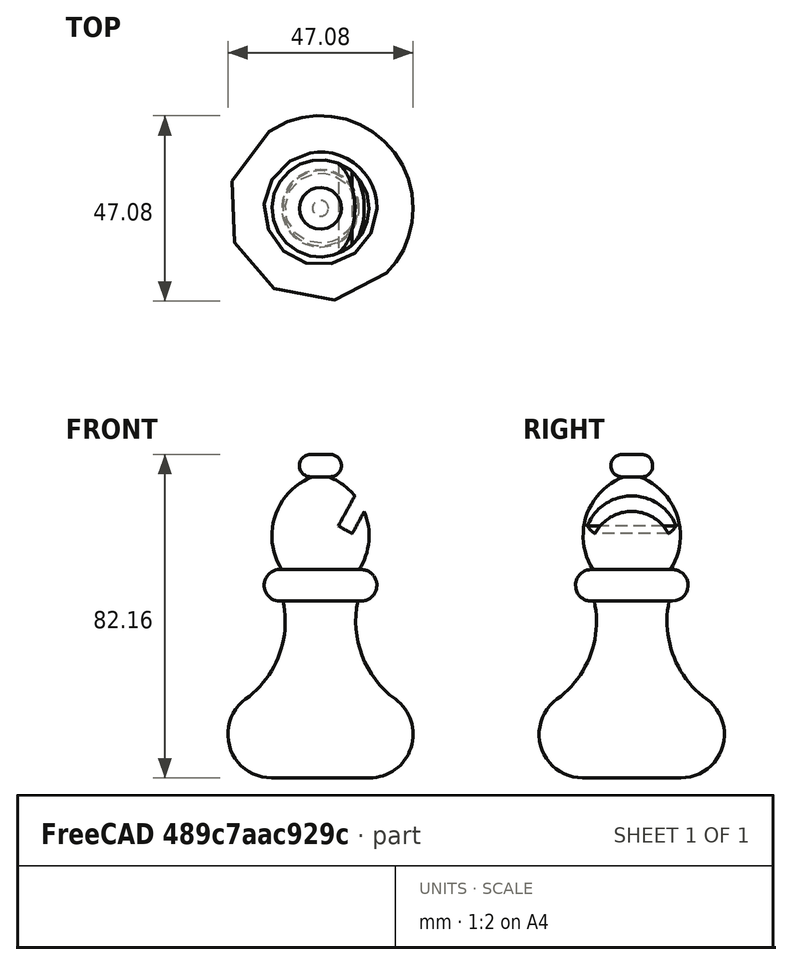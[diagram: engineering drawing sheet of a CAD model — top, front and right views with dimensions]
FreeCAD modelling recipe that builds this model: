
FCSTD DOCUMENT  (FreeCAD 0.16R)
Label: Bishop1
License: All rights reserved
LicenseURL: http://en.wikipedia.org/wiki/All_rights_reserved
objects: Sketcher::SketchObject×2, PartDesign::Revolution×1, PartDesign::Pad×1, Part::Cut×1, Mesh::Feature×1
note: 7 computed .brp shape members not serialized (recipe doc carries the construction recipe); baked Part::Feature solids carry a one-line shape summary decoded from their .brp

FEATURE [Sketcher::SketchObject] Sketch
  Placement = pos=(0,0,0) rot=(-1,0,0;4.71239rad)
  sketch-geometry (9):
    g0: ArcOfCircle CenterX=-3.65574 CenterY=41.525 CenterZ=0 NormalX=0 NormalY=0 NormalZ=1 Radius=16 StartAngle=5.71293 EndAngle=7.49269
    g1: ArcOfCircle CenterX=10.3244 CenterY=28.9203 CenterZ=0 NormalX=0 NormalY=0 NormalZ=1 Radius=4 StartAngle=4.51243 EndAngle=7.98232
    g2: ArcOfCircle CenterX=33.4264 CenterY=19.7584 CenterZ=0 NormalX=0 NormalY=0 NormalZ=1 Radius=24.4646 StartAngle=2.92567 EndAngle=4.08172
    g3: ArcOfCircle CenterX=12.4756 CenterY=-8.93581 CenterZ=0 NormalX=0 NormalY=0 NormalZ=1 Radius=11.0642 StartAngle=4.71239 EndAngle=7.22331
    g4: LineSegment StartX=0 StartY=-20 StartZ=0 EndX=12.4756 EndY=-20 EndZ=0
    g5: ArcOfCircle CenterX=2.5 CenterY=59.3249 CenterZ=0 NormalX=0 NormalY=0 NormalZ=1 Radius=2.8329 StartAngle=4.71239 EndAngle=7.85398
    g6: LineSegment StartX=2 StartY=56.492 StartZ=0 EndX=2.5 EndY=56.492 EndZ=0
    g7: LineSegment StartX=0 StartY=62.1578 StartZ=0 EndX=2.5 EndY=62.1578 EndZ=0
    g8: LineSegment StartX=0 StartY=-20 StartZ=0 EndX=0 EndY=62.1578 EndZ=0
  constraints (26):
    c: Coincident(g2,g1)
    c: Coincident(g2,g3)
    c: Horizontal(g4)
    c: PointOnObject(g4,g-2)
    c: Coincident(g4,g3)
    c: Tangent(g4,g3)
    c: Tangent(g3,g2)
    c: Coincident(g0,g1)
    c: Tangent(g6,g5) = -1.5708
    c: Tangent(g7,g5) = 1.5708
    c: Horizontal(g6)
    c: Coincident(g6,g0)
    c: PointOnObject(g7,g-2)
    c: Vertical(g8)
    c: Coincident(g8,g7)
    c: Coincident(g4,g8)
    c: Horizontal(g7)
    c: Radius(g1) = 4
    c: Radius(g0) = 16
    c: DistanceX(g0) = 2
    c: DistanceX(g2) = 19
    c: PointOnObject(g2,g-1)
    c: DistanceY(g1) = 25
    c: DistanceY(g0) = 32.8874
    c: DistanceX(g5) = 2.5
    c: DistanceY(g4) = -20
FEATURE [PartDesign::Revolution] Revolution
  Angle = 360
  Axis = (0,0,1)
  Base = (0,0,0)
  Placement = pos=(0,0,0) rot=(-1,0,0;4.71239rad)
  ReferenceAxis = -> Sketch [V_Axis]
  Reversed = true
  Sketch = -> Sketch
FEATURE [Sketcher::SketchObject] Sketch001
  Placement = pos=(0,0,0) rot=(-1,0,0;4.71239rad)
  sketch-geometry (4):
    g0: LineSegment StartX=12.4992 StartY=58.5281 StartZ=0 EndX=4.54 EndY=44 EndZ=0
    g1: LineSegment StartX=4.54 StartY=44 StartZ=0 EndX=8.04805 EndY=42.0781 EndZ=0
    g2: LineSegment StartX=8.04805 StartY=42.0781 StartZ=0 EndX=16.0072 EndY=56.6062 EndZ=0
    g3: LineSegment StartX=16.0072 StartY=56.6062 StartZ=0 EndX=12.4992 EndY=58.5281 EndZ=0
  constraints (12):
    c: Coincident(g0,g1)
    c: Coincident(g1,g2)
    c: Coincident(g2,g3)
    c: Coincident(g3,g0)
    c: Parallel(g3,g1)
    c: Parallel(g2,g0)
    c: Perpendicular(g0,g3)
    c: Angle(g0) = -2.07199
    c: DistanceX(g0) = 4.54
    c: DistanceY(g0) = 44
    c: Distance(g2) = 16.5654
    c: Distance(g1) = 4
FEATURE [PartDesign::Pad] Pad
  Length = 25
  Length2 = 100
  Midplane = true
  Placement = pos=(0,0,0) rot=(-1,0,0;4.71239rad)
  Sketch = -> Sketch001
  Type = 0
FEATURE [Part::Cut] Cut
  Base = -> Revolution
  Tool = -> Pad
FEATURE [Mesh::Feature] Mesh  label="Cut (Meshed)"
